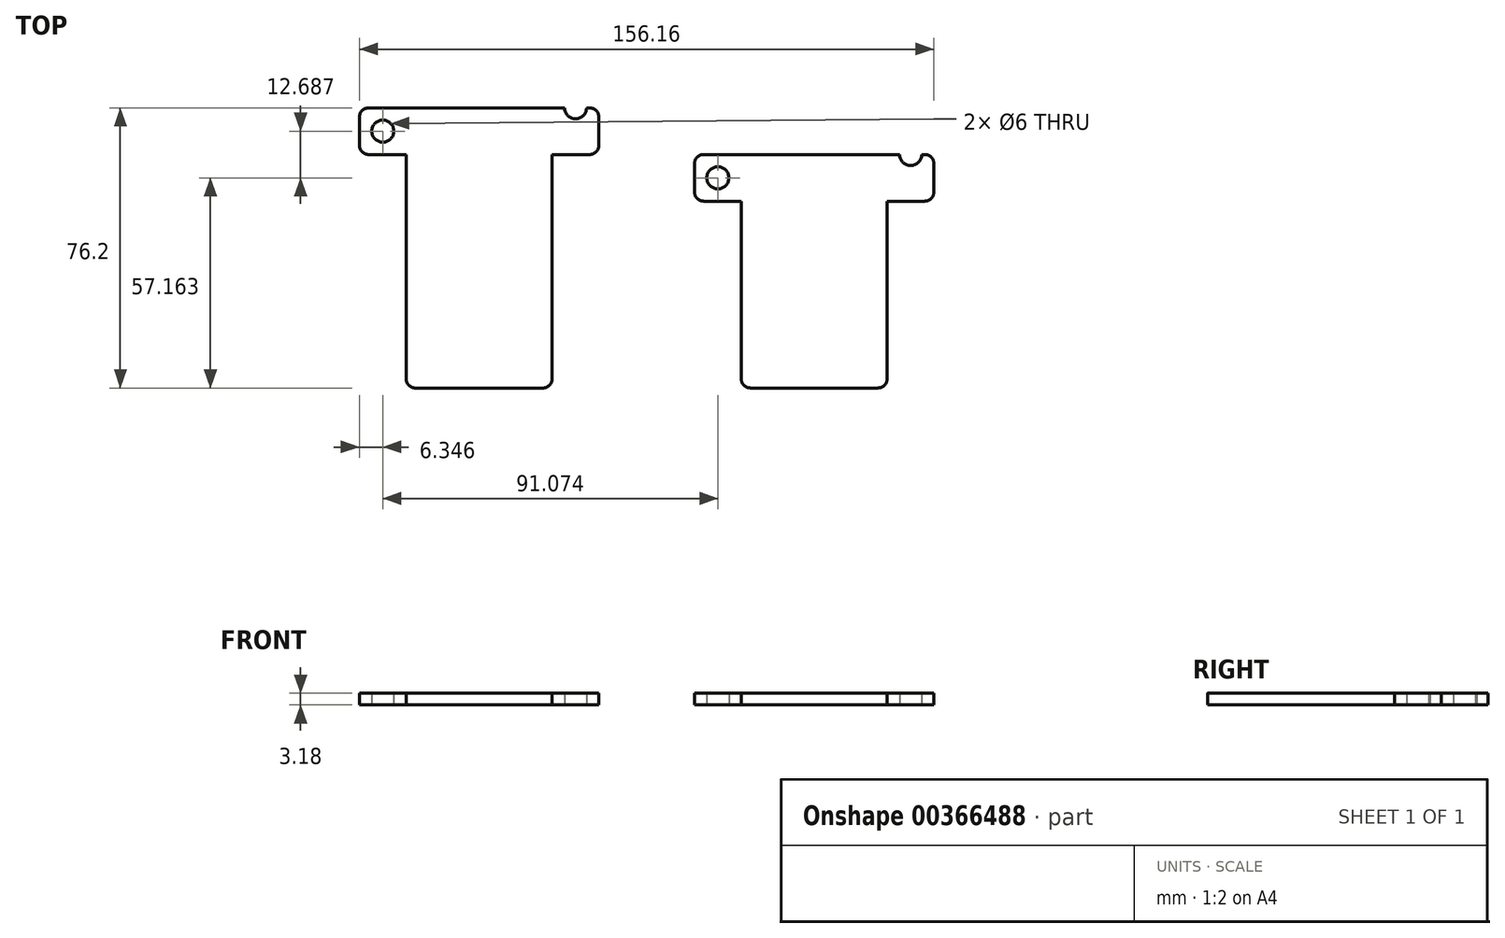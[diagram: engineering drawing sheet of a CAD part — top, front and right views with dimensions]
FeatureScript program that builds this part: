
annotation { "Feature Type Name" : "Feature", "Feature Type Description" : "" }
export const myFeature = defineFeature(function(context is Context, id is Id, definition is map)
    precondition{}
    {
        {
            var Q0;
            Q0=qCreatedBy(makeId("Top.planeOp"),FACE);
            var sketch = newSketch(context, id + "F0", { "sketchPlane" : qUnion([Q0])});
            skLineSegment(sketch, "E0.top", {"start": v(-17.3, -31.75) * mm, "end": v(17.3, -31.75) * mm});
            skLineSegment(sketch, "E0.left", {"start": v(-19.84, 31.75) * mm, "end": v(-19.84, -29.21) * mm});
            skLineSegment(sketch, "E0.right", {"start": v(19.84, 31.75) * mm, "end": v(19.84, -29.21) * mm});
            skPoint(sketch, "E0.middle", {"position": v(0, 0) * mm});
            skLineSegment(sketch, "E1", {"start": v(19.84, 31.75) * mm, "end": v(30, 31.75) * mm});
            skLineSegment(sketch, "E2", {"start": v(-19.84, 31.75) * mm, "end": v(-30, 31.75) * mm});
            skLineSegment(sketch, "E3", {"start": v(-32.54, 34.29) * mm, "end": v(-32.54, 41.9) * mm});
            skLineSegment(sketch, "E4", {"start": v(32.54, 34.3) * mm, "end": v(32.54, 41.91) * mm});
            skCircle(sketch, "E5", {"center": v(-26.2, 38.1) * mm, "radius": 3 * mm});
            skPoint(sketch, "E6.visualSharp", {"position": v(-32.54, 44.45) * mm});
            skArc(sketch, "E6.filletArc", {"start": v(-30, 44.45) * mm, "mid": v(-31.8, 43.7) * mm, "end": v(-32.54, 41.9) * mm});
            skPoint(sketch, "E7.visualSharp", {"position": v(-32.54, 31.75) * mm});
            skArc(sketch, "E7.filletArc", {"start": v(-32.54, 34.29) * mm, "mid": v(-31.8, 32.5) * mm, "end": v(-30, 31.75) * mm});
            skPoint(sketch, "E8.visualSharp", {"position": v(32.54, 31.75) * mm});
            skArc(sketch, "E8.filletArc", {"start": v(30, 31.75) * mm, "mid": v(31.8, 32.5) * mm, "end": v(32.54, 34.3) * mm});
            skPoint(sketch, "E9.visualSharp", {"position": v(32.54, 44.45) * mm});
            skArc(sketch, "E9.filletArc", {"start": v(32.54, 41.91) * mm, "mid": v(31.8, 43.7) * mm, "end": v(30, 44.45) * mm});
            skPoint(sketch, "E10.visualSharp", {"position": v(-19.84, -31.75) * mm});
            skArc(sketch, "E10.filletArc", {"start": v(-19.84, -29.21) * mm, "mid": v(-19.1, -31) * mm, "end": v(-17.3, -31.75) * mm});
            skPoint(sketch, "E11.visualSharp", {"position": v(19.84, -31.75) * mm});
            skArc(sketch, "E11.filletArc", {"start": v(17.3, -31.75) * mm, "mid": v(19.1, -31) * mm, "end": v(19.84, -29.21) * mm});
            skPoint(sketch, "E12", {"position": v(26.2, 44.45) * mm});
            skArc(sketch, "E13", {"start": v(29.2, 44.45) * mm, "mid": v(26.2, 41.45) * mm, "end": v(23.2, 44.45) * mm});
            skLineSegment(sketch, "E14", {"start": v(29.2, 44.45) * mm, "end": v(30, 44.45) * mm});
            skLineSegment(sketch, "E15", {"start": v(-30, 44.45) * mm, "end": v(23.2, 44.45) * mm});
            skSolve(sketch);
        }
        {
            var Q0;
            Q0=makeQuery(id+"F0.imprint","IMPRINT",FACE,{"disambiguationData":[TD([[makeQuery(id+"F0.imprint","IMPRINT",EDGE,{"derivedFrom":sQuery(id+"F0.wireOp",EDGE,"E0.top")}),1.0]])]});
            extrude(context, id + "F1", {"entities" : qUnion([Q0]), "depth" : 3.17 * mm});
        }
        {
            var Q0;
            Q0=qCreatedBy(makeId("Top.planeOp"),FACE);
            var sketch = newSketch(context, id + "F2", { "sketchPlane" : qUnion([Q0])});
            skLineSegment(sketch, "E16.top", {"start": v(73.77, -31.74) * mm, "end": v(108.38, -31.74) * mm});
            skLineSegment(sketch, "E16.left", {"start": v(71.23, 19.06) * mm, "end": v(71.23, -29.2) * mm});
            skLineSegment(sketch, "E16.right", {"start": v(110.92, 19.06) * mm, "end": v(110.92, -29.2) * mm});
            skPoint(sketch, "E16.middle", {"position": v(91.07, -6.34) * mm});
            skLineSegment(sketch, "E17", {"start": v(110.92, 19.06) * mm, "end": v(121.08, 19.06) * mm});
            skLineSegment(sketch, "E18", {"start": v(71.23, 19.06) * mm, "end": v(61.07, 19.06) * mm});
            skLineSegment(sketch, "E19", {"start": v(58.53, 21.6) * mm, "end": v(58.53, 29.22) * mm});
            skLineSegment(sketch, "E20", {"start": v(123.62, 21.6) * mm, "end": v(123.62, 29.22) * mm});
            skCircle(sketch, "E21", {"center": v(64.88, 25.41) * mm, "radius": 3 * mm});
            skPoint(sketch, "E22.visualSharp", {"position": v(58.53, 31.76) * mm});
            skArc(sketch, "E22.filletArc", {"start": v(61.07, 31.76) * mm, "mid": v(59.27, 31.02) * mm, "end": v(58.53, 29.22) * mm});
            skPoint(sketch, "E23.visualSharp", {"position": v(58.53, 19.06) * mm});
            skArc(sketch, "E23.filletArc", {"start": v(58.53, 21.6) * mm, "mid": v(59.27, 19.8) * mm, "end": v(61.07, 19.06) * mm});
            skPoint(sketch, "E24.visualSharp", {"position": v(123.62, 19.06) * mm});
            skArc(sketch, "E24.filletArc", {"start": v(121.08, 19.06) * mm, "mid": v(122.87, 19.8) * mm, "end": v(123.62, 21.6) * mm});
            skPoint(sketch, "E25.visualSharp", {"position": v(123.62, 31.76) * mm});
            skArc(sketch, "E25.filletArc", {"start": v(123.62, 29.22) * mm, "mid": v(122.87, 31.02) * mm, "end": v(121.08, 31.76) * mm});
            skPoint(sketch, "E26.visualSharp", {"position": v(71.23, -31.74) * mm});
            skArc(sketch, "E26.filletArc", {"start": v(71.23, -29.2) * mm, "mid": v(71.97, -31) * mm, "end": v(73.77, -31.74) * mm});
            skPoint(sketch, "E27.visualSharp", {"position": v(110.92, -31.74) * mm});
            skArc(sketch, "E27.filletArc", {"start": v(108.38, -31.74) * mm, "mid": v(110.17, -31) * mm, "end": v(110.92, -29.2) * mm});
            skPoint(sketch, "E28", {"position": v(117.27, 31.76) * mm});
            skArc(sketch, "E29", {"start": v(120.27, 31.76) * mm, "mid": v(117.27, 28.76) * mm, "end": v(114.27, 31.76) * mm});
            skLineSegment(sketch, "E30", {"start": v(120.27, 31.76) * mm, "end": v(121.08, 31.76) * mm});
            skLineSegment(sketch, "E31", {"start": v(61.07, 31.76) * mm, "end": v(114.27, 31.76) * mm});
            skSolve(sketch);
        }
        {
            var Q0;
            Q0 = qSketchRegion(id + "F2", true);
            extrude(context, id + "F3", {"entities" : qUnion([Q0]), "depth" : 3.17 * mm});
        }
    });
